# Revit family: ITK_Вставка для 2 модулей Keystone Jack_Настенный кабель-канал_IP20
name_source: partatom
category: Обобщенные модели
units: mm (PartAtom-declared; Revit-internal decimal feet)

## family parameters
Всегда вертикально = Да
Может служить основой для арматурных стержней = Нет
На основе рабочей плоскости = Нет
Общий = Нет
При загрузке вырезать с полостями = Нет
Размер круглого соединителя = Использовать диаметр
Тип детали = Нормальный
Точка расчета площади = Нет

## types (1)
- CS6-22M
    ADSK_URL страницы изделия = https://www.itk-group.ru
    ADSK_Версия Revit = 2019
    ADSK_Версия семейства = 1.0
    ADSK_Группирование = I. ЩИТЫ И ПУЛЬТЫ
    ADSK_Единица измерения = шт
    ADSK_Завод-изготовитель = IEK
    ADSK_Код изделия = CS6-22M
    ADSK_Масса = 0
    ADSK_Материал наименование = Пластик
    ADSK_Наименование = ITK Вставка 45х45мм для 2 мод. Keystone Jack с маркером
    IEK_URL = https://www.itk-group.ru
    IEK_Описание = Соответствие международным стандартам качества, что обеспечивает совместимость с компонентами для СКС и с кабелем других производителей.
Изготовлены из высококачественных негорючих материалов и отличаются надежностью и удобством эксплуатации.
    IEK_Цена за единицу = 69.2
    KSI_CMa_Строительные материалы = 01.7.14.03
    URL = https://www.iek.ru
    Высота = 45 мм
    Глубина = 22 мм
    Изготовитель = ITK
    Материал = Пластик белый
    Степень защиты = IP20
    Ширина = 45 мм
